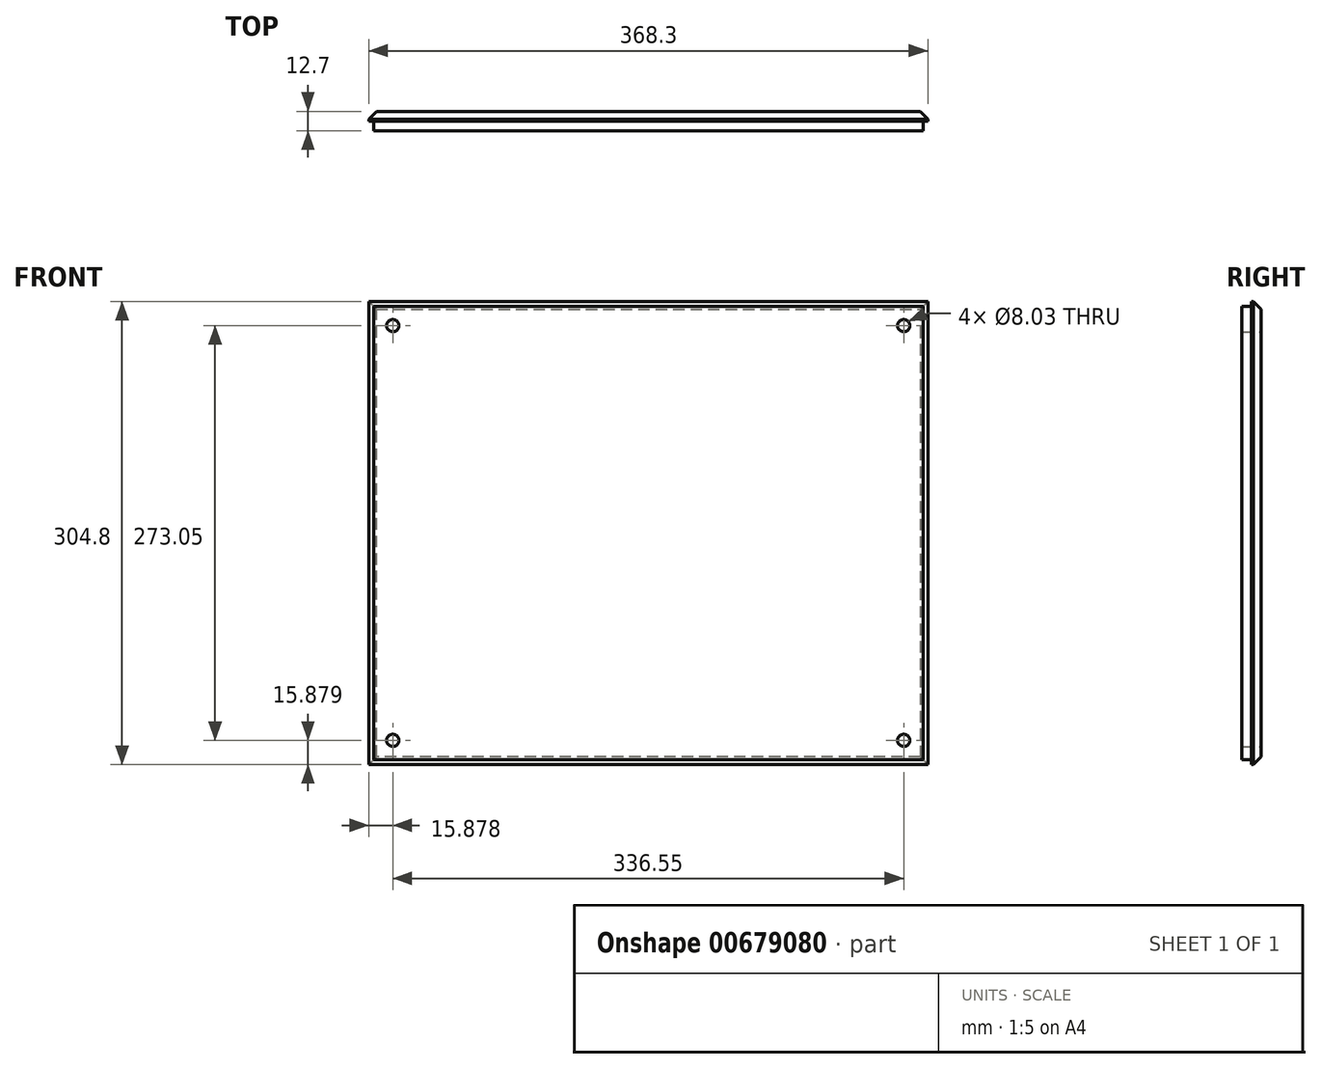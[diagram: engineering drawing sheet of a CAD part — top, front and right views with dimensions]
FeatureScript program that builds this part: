
annotation { "Feature Type Name" : "Feature", "Feature Type Description" : "" }
export const myFeature = defineFeature(function(context is Context, id is Id, definition is map)
    precondition{}
    {
        {
            var Q0;
            Q0=qCreatedBy(makeId("Front.planeOp"),FACE);
            var sketch = newSketch(context, id + "F0", { "sketchPlane" : qUnion([Q0])});
            skLineSegment(sketch, "E0.bottom", {"start": v(-184.17, -152.44) * mm, "end": v(184.13, -152.44) * mm});
            skLineSegment(sketch, "E0.top", {"start": v(-184.17, 152.36) * mm, "end": v(184.13, 152.36) * mm});
            skLineSegment(sketch, "E0.left", {"start": v(-184.17, -152.44) * mm, "end": v(-184.17, 152.36) * mm});
            skLineSegment(sketch, "E0.right", {"start": v(184.13, -152.44) * mm, "end": v(184.13, 152.36) * mm});
            skLineSegment(sketch, "E1.bottom", {"start": v(-181, 149.19) * mm, "end": v(180.96, 149.19) * mm});
            skLineSegment(sketch, "E1.top", {"start": v(-181, -149.26) * mm, "end": v(180.96, -149.26) * mm});
            skLineSegment(sketch, "E1.left", {"start": v(-181, 149.19) * mm, "end": v(-181, -149.26) * mm});
            skLineSegment(sketch, "E1.right", {"start": v(180.96, 149.19) * mm, "end": v(180.96, -149.26) * mm});
            skCircle(sketch, "E2", {"center": v(-168.3, 136.49) * mm, "radius": 4.02 * mm});
            skCircle(sketch, "E3", {"center": v(-168.3, -136.56) * mm, "radius": 4.02 * mm});
            skCircle(sketch, "E4", {"center": v(168.26, -136.56) * mm, "radius": 4.02 * mm});
            skCircle(sketch, "E5", {"center": v(168.26, 136.49) * mm, "radius": 4.02 * mm});
            skSolve(sketch);
        }
        {
            var Q0;
            Q0=makeQuery(id+"F0.imprint","IMPRINT",FACE,{"disambiguationData":[TD([[makeQuery(id+"F0.imprint","IMPRINT",EDGE,{"derivedFrom":sQuery(id+"F0.wireOp",EDGE,"E1.bottom")}),-1.0]])]});
            extrude(context, id + "F1", {"entities" : qUnion([Q0]), "depth" : 6.35 * mm, "offsetDistance" : 25.4 * mm});
        }
        {
            var Q0;
            Q0=makeQuery(id+"F0.imprint","IMPRINT",FACE,{"disambiguationData":[TD([[makeQuery(id+"F0.imprint","IMPRINT",EDGE,{"derivedFrom":sQuery(id+"F0.wireOp",EDGE,"E0.bottom")}),1.0]])]});
            var Q1;
            Q1=makeQuery(id+"F0.imprint","IMPRINT",FACE,{"disambiguationData":[TD([[makeQuery(id+"F0.imprint","IMPRINT",EDGE,{"derivedFrom":sQuery(id+"F0.wireOp",EDGE,"E1.bottom")}),-1.0]])]});
            extrude(context, id + "F2", {"entities" : qUnion([Q0, Q1]), "operationType" : NewBodyOperationType.ADD, "depth" : -6.35 * mm, "offsetDistance" : 25.4 * mm});
        }
        {
            var Q0;
            Q0=makeQuery(id+"F2.opExtrude","CAP_EDGE",EDGE,{"disambiguationData":[OSD([sQuery(id+"F0.wireOp",EDGE,"E0.top")])],"isStart":false});
            var Q1;
            Q1=makeQuery(id+"F2.opExtrude","CAP_EDGE",EDGE,{"disambiguationData":[OSD([sQuery(id+"F0.wireOp",EDGE,"E0.right")])],"isStart":false});
            var Q2;
            Q2=makeQuery(id+"F2.opExtrude","CAP_EDGE",EDGE,{"disambiguationData":[OSD([sQuery(id+"F0.wireOp",EDGE,"E0.bottom")])],"isStart":false});
            var Q3;
            Q3=makeQuery(id+"F2.opExtrude","CAP_EDGE",EDGE,{"disambiguationData":[OSD([sQuery(id+"F0.wireOp",EDGE,"E0.left")])],"isStart":false});
            chamfer(context, id + "F3", {"entities" : qUnion([Q0, Q1, Q2, Q3]), "width" : 5.08 * mm, "tangentPropagation" : true});
        }
    });
